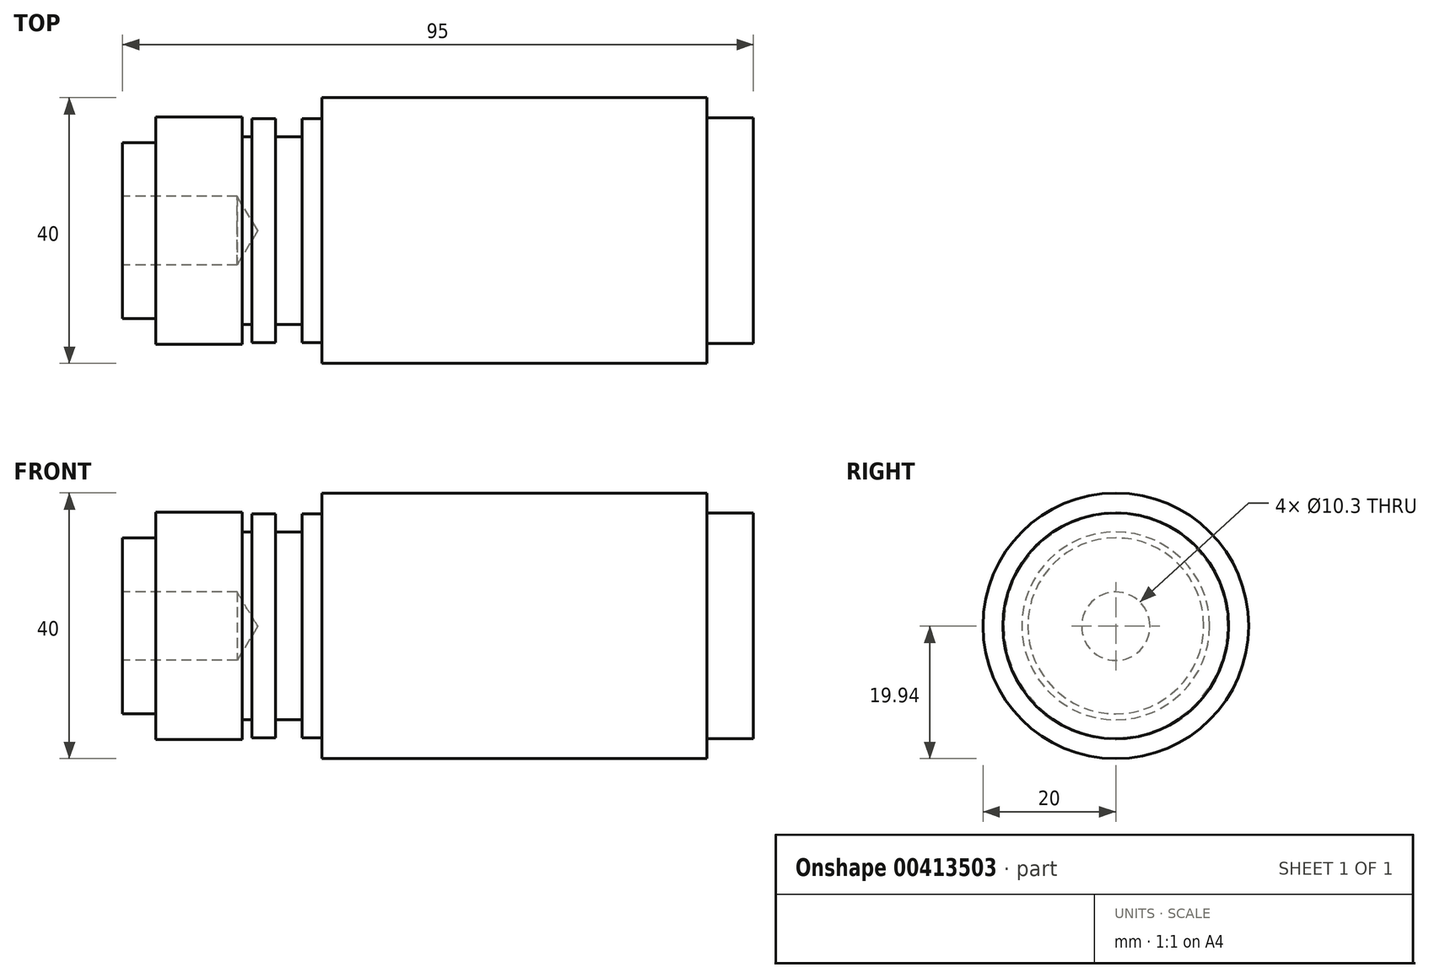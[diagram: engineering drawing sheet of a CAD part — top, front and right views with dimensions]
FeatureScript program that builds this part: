
annotation { "Feature Type Name" : "Feature", "Feature Type Description" : "" }
export const myFeature = defineFeature(function(context is Context, id is Id, definition is map)
    precondition{}
    {
        {
            var Q0;
            Q0=qCreatedBy(makeId("Front.planeOp"),FACE);
            var sketch = newSketch(context, id + "F0", { "sketchPlane" : qUnion([Q0])});
            skLineSegment(sketch, "E0", {"start": v(-66.9, 0.06) * mm, "end": v(28.1, 0.06) * mm});
            skLineSegment(sketch, "E1", {"start": v(-66.9, 0.06) * mm, "end": v(-66.9, 13.3) * mm});
            skLineSegment(sketch, "E2", {"start": v(-66.9, 13.3) * mm, "end": v(-61.9, 13.3) * mm});
            skLineSegment(sketch, "E3", {"start": v(-61.9, 13.3) * mm, "end": v(-61.9, 17.15) * mm});
            skLineSegment(sketch, "E4", {"start": v(-61.9, 17.15) * mm, "end": v(-48.9, 17.15) * mm});
            skLineSegment(sketch, "E5", {"start": v(-48.9, 17.15) * mm, "end": v(-48.9, 14.2) * mm});
            skLineSegment(sketch, "E6", {"start": v(-48.9, 14.2) * mm, "end": v(-47.4, 14.2) * mm});
            skLineSegment(sketch, "E7", {"start": v(-47.4, 14.2) * mm, "end": v(-47.4, 16.9) * mm});
            skLineSegment(sketch, "E8", {"start": v(-47.4, 16.9) * mm, "end": v(-43.9, 16.9) * mm});
            skLineSegment(sketch, "E9", {"start": v(-43.9, 16.9) * mm, "end": v(-43.9, 14.2) * mm});
            skLineSegment(sketch, "E10", {"start": v(-43.9, 14.2) * mm, "end": v(-39.9, 14.2) * mm});
            skLineSegment(sketch, "E11", {"start": v(-39.9, 14.2) * mm, "end": v(-39.9, 16.9) * mm});
            skLineSegment(sketch, "E12", {"start": v(-36.9, 20.06) * mm, "end": v(21.1, 20.06) * mm});
            skLineSegment(sketch, "E13", {"start": v(21.1, 20.06) * mm, "end": v(21.1, 17.06) * mm});
            skLineSegment(sketch, "E14", {"start": v(21.1, 17.06) * mm, "end": v(28.1, 17.06) * mm});
            skLineSegment(sketch, "E15", {"start": v(28.1, 17.06) * mm, "end": v(28.1, 0.06) * mm});
            skLineSegment(sketch, "E16", {"start": v(-39.9, 16.9) * mm, "end": v(-36.9, 16.9) * mm});
            skLineSegment(sketch, "E17", {"start": v(-36.9, 16.9) * mm, "end": v(-36.9, 20.06) * mm});
            skLineSegment(sketch, "E18", {"start": v(-72.34, 0) * mm, "end": v(36.35, 0) * mm, "construction": true});
            skSolve(sketch);
        }
        {
            var Q0;
            Q0=makeQuery(id+"F0.imprint","IMPRINT",FACE,{"disambiguationData":[TD([[makeQuery(id+"F0.imprint","IMPRINT",EDGE,{"derivedFrom":sQuery(id+"F0.wireOp",EDGE,"E0")}),1.0]])]});
            var Q1;
            Q1=sQuery(id+"F0.wireOp",EDGE,"E0");
            revolve(context, id + "F1", {"entities" : qUnion([Q0]), "axis" : qUnion([Q1]), "revolveType" : RevolveType.FULL});
        }
        {
            var Q0;
            Q0=makeQuery(id+"F1.opRevolve","SWEPT_FACE",FACE,{"disambiguationData":[OSD([sQuery(id+"F0.wireOp",EDGE,"E1")])]});
            var sketch = newSketch(context, id + "F2", { "sketchPlane" : qUnion([Q0])});
            skPoint(sketch, "E19", {"position": v(0, 0) * mm});
            skSolve(sketch);
        }
        {
            var Q0;
            Q0=sQuery(id+"F2.wireOp",VERTEX,"E19");
            var Q1;
            Q1=makeQuery(id+"F1.opRevolve","SWEPT_BODY",BODY,{"disambiguationData":[OSD([sQuery(id+"F0.wireOp",EDGE,"E0"),sQuery(id+"F0.wireOp",EDGE,"E1"),sQuery(id+"F0.wireOp",EDGE,"E2"),sQuery(id+"F0.wireOp",EDGE,"E3"),sQuery(id+"F0.wireOp",EDGE,"E4"),sQuery(id+"F0.wireOp",EDGE,"E5"),sQuery(id+"F0.wireOp",EDGE,"E6"),sQuery(id+"F0.wireOp",EDGE,"E7"),sQuery(id+"F0.wireOp",EDGE,"E8"),sQuery(id+"F0.wireOp",EDGE,"E9"),sQuery(id+"F0.wireOp",EDGE,"E10"),sQuery(id+"F0.wireOp",EDGE,"E11"),sQuery(id+"F0.wireOp",EDGE,"E12"),sQuery(id+"F0.wireOp",EDGE,"E13"),sQuery(id+"F0.wireOp",EDGE,"E14"),sQuery(id+"F0.wireOp",EDGE,"E15"),sQuery(id+"F0.wireOp",EDGE,"E16"),sQuery(id+"F0.wireOp",EDGE,"E17")])]});
            hole(context, id + "F3", {"style" : HoleStyle.SIMPLE, "endStyle" : HoleEndStyle.BLIND, "standardTappedOrClearance" : lookupTablePath({ "standard" : "ISO", "engagement" : "75%", "pitch" : "1.75 mm", "size" : "M12", "type" : "Tapped" }), "standardBlindInLast" : lookupTablePath({ "standard" : "ISO", "engagement" : "75%", "pitch" : "1.75 mm", "size" : "M12", "type" : "Tapped" }), "holeDiameter" : 10.3 * mm, "showTappedDepth" : true, "holeDepth" : 17.25 * mm, "isTappedThrough" : true, "tappedDepth" : 12 * mm, "tapClearance" : 3, "locations" : qUnion([Q0]), "scope" : qUnion([Q1]), "majorDiameter" : 12 * mm});
        }
    });
